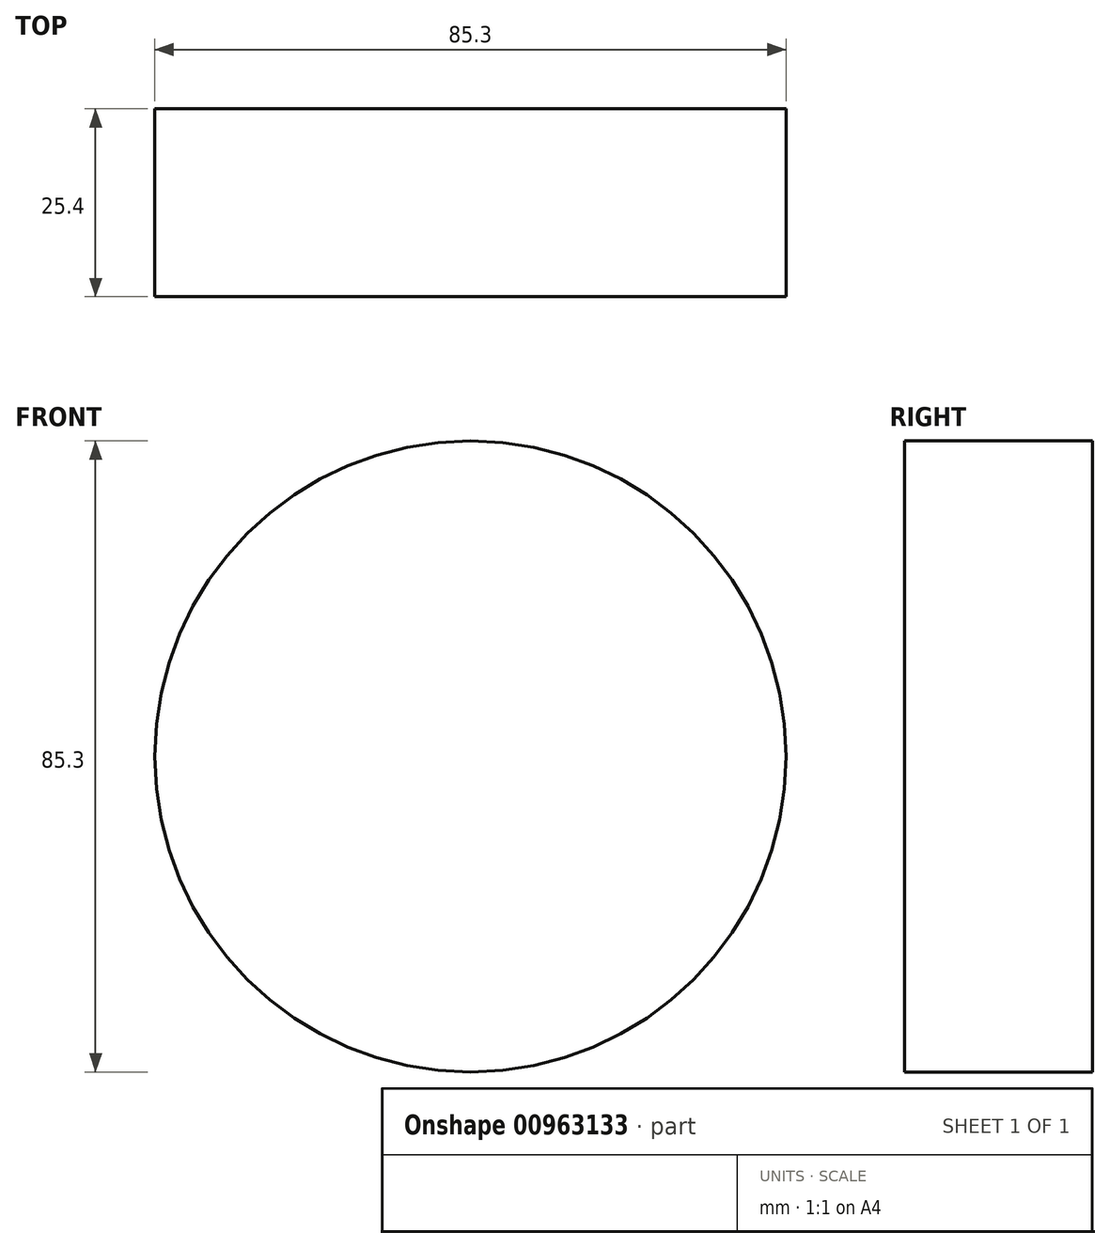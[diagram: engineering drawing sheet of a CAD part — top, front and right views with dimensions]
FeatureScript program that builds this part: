
annotation { "Feature Type Name" : "Feature", "Feature Type Description" : "" }
export const myFeature = defineFeature(function(context is Context, id is Id, definition is map)
    precondition{}
    {
        {
            var Q0;
            Q0=qCreatedBy(makeId("Front.planeOp"),FACE);
            var sketch = newSketch(context, id + "F0", { "sketchPlane" : qUnion([Q0])});
            skCircle(sketch, "E0", {"center": v(0, 0) * mm, "radius": 42.65 * mm});
            skSolve(sketch);
        }
        {
            var Q0;
            Q0=makeQuery(id+"F0.imprint","IMPRINT",FACE,{"disambiguationData":[TD([[makeQuery(id+"F0.imprint","IMPRINT",EDGE,{"derivedFrom":sQuery(id+"F0.wireOp",EDGE,"E0")}),1.0]])]});
            extrude(context, id + "F1", {"entities" : qUnion([Q0]), "depth" : 25.4 * mm, "offsetDistance" : 25.4 * mm});
        }
    });
